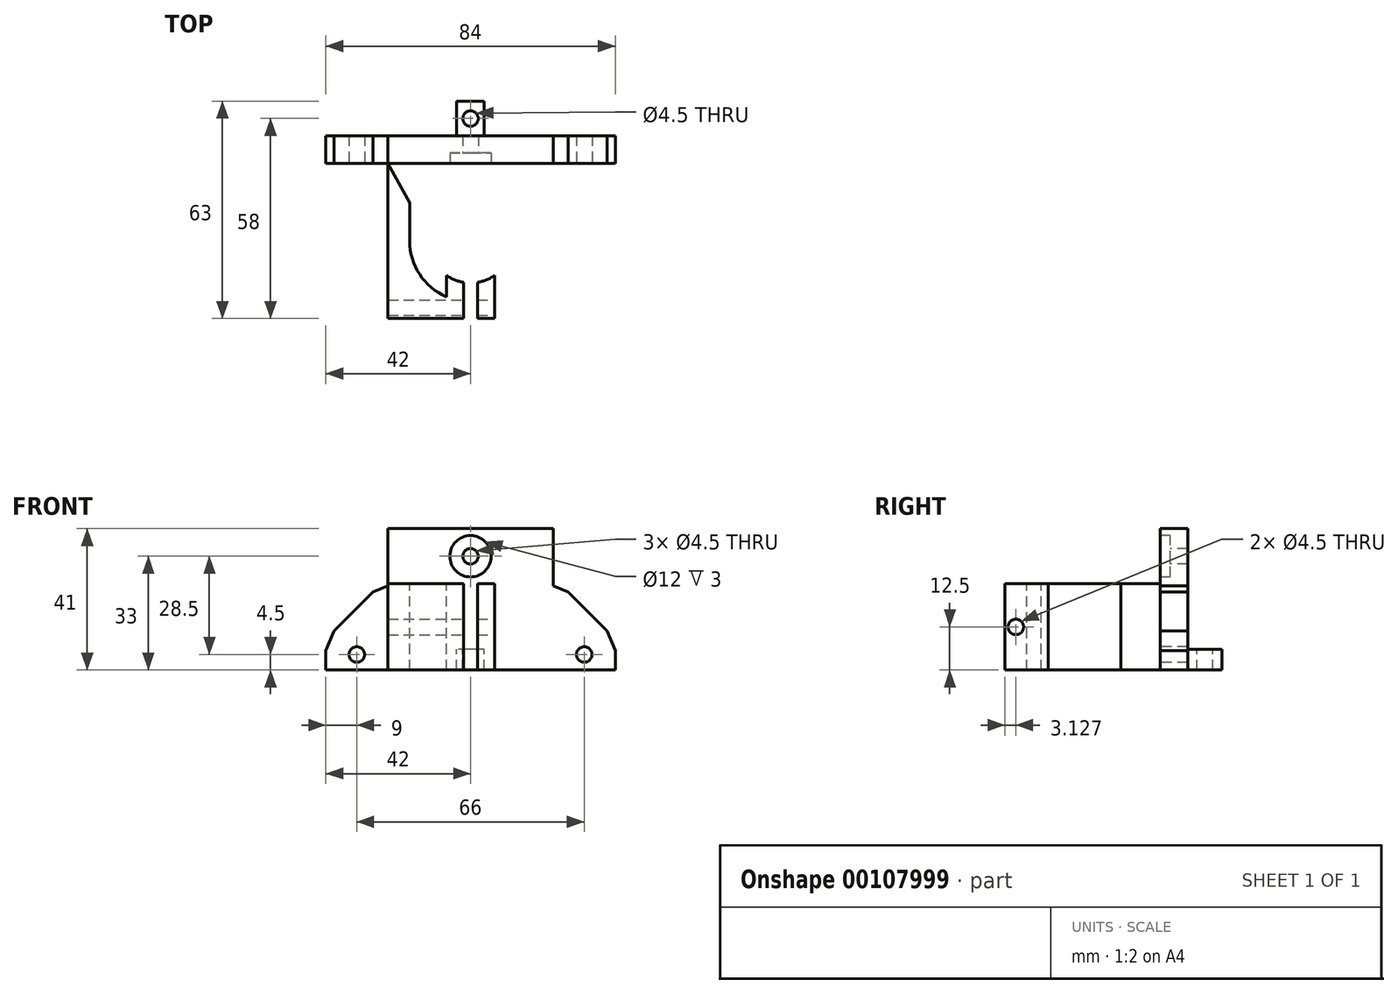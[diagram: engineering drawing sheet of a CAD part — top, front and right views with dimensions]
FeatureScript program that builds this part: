
annotation { "Feature Type Name" : "Feature", "Feature Type Description" : "" }
export const myFeature = defineFeature(function(context is Context, id is Id, definition is map)
    precondition{}
    {
        {
            var Q0;
            Q0=qCreatedBy(makeId("Front.planeOp"),FACE);
            var sketch = newSketch(context, id + "F0", { "sketchPlane" : qUnion([Q0])});
            skLineSegment(sketch, "E0.bottom", {"start": v(0, 0) * mm, "end": v(48, 0) * mm});
            skLineSegment(sketch, "E0.top", {"start": v(0, 49) * mm, "end": v(48, 49) * mm});
            skLineSegment(sketch, "E0.left", {"start": v(0, 0) * mm, "end": v(0, 49) * mm});
            skLineSegment(sketch, "E0.right", {"start": v(48, 0) * mm, "end": v(48, 49) * mm});
            skSolve(sketch);
        }
        {
            var Q0;
            Q0 = qSketchRegion(id + "F0", true);
            extrude(context, id + "F1", {"entities" : qUnion([Q0]), "depth" : (70 - 25 + 8) * mm});
        }
        {
            var Q0;
            Q0=makeQuery(id+"F1.opExtrude","CAP_FACE",FACE,{"disambiguationData":[OSD([sQuery(id+"F0.wireOp",EDGE,"E0.bottom"),sQuery(id+"F0.wireOp",EDGE,"E0.top"),sQuery(id+"F0.wireOp",EDGE,"E0.left"),sQuery(id+"F0.wireOp",EDGE,"E0.right")])],"isStart":false});
            var sketch = newSketch(context, id + "F2", { "sketchPlane" : qUnion([Q0])});
            skLineSegment(sketch, "E1.bottom", {"start": v(0, 49) * mm, "end": v(48, 49) * mm});
            skLineSegment(sketch, "E1.top", {"start": v(0, 25) * mm, "end": v(48, 25) * mm});
            skLineSegment(sketch, "E1.left", {"start": v(0, 49) * mm, "end": v(0, 25) * mm});
            skLineSegment(sketch, "E1.right", {"start": v(48, 49) * mm, "end": v(48, 25) * mm});
            skSolve(sketch);
        }
        {
            var Q0;
            Q0 = qSketchRegion(id + "F2", true);
            extrude(context, id + "F3", {"entities" : qUnion([Q0]), "operationType" : NewBodyOperationType.REMOVE, "oppositeDirection" : true, "depth" : 45 * mm});
        }
        {
            var Q0;
            Q0=makeQuery(id+"F3.boolean.opBoolean","COPY",FACE,{"derivedFrom":makeQuery(id+"F3.opExtrude","SWEPT_FACE",FACE,{"disambiguationData":[OSD([sQuery(id+"F2.wireOp",EDGE,"E1.top")])]})});
            var sketch = newSketch(context, id + "F4", { "sketchPlane" : qUnion([Q0])});
            skCircle(sketch, "E2", {"center": v(24, -30.5) * mm, "radius": 12.2 * mm});
            skLineSegment(sketch, "E3", {"start": v(24, -8) * mm, "end": v(24, -53) * mm, "construction": true});
            skLineSegment(sketch, "E4", {"start": v(0, -30.5) * mm, "end": v(48, -30.5) * mm, "construction": true});
            skLineSegment(sketch, "E5.bottom", {"start": v(22, -53) * mm, "end": v(26, -53) * mm});
            skLineSegment(sketch, "E5.top", {"start": v(22, -42.53) * mm, "end": v(26, -42.53) * mm});
            skLineSegment(sketch, "E5.left", {"start": v(22, -53) * mm, "end": v(22, -42.53) * mm});
            skLineSegment(sketch, "E5.right", {"start": v(26, -53) * mm, "end": v(26, -42.53) * mm});
            skLineSegment(sketch, "E6", {"start": v(17, -40.5) * mm, "end": v(31, -40.5) * mm});
            skLineSegment(sketch, "E7.bottom", {"start": v(17, -53) * mm, "end": v(31, -53) * mm});
            skLineSegment(sketch, "E7.left", {"start": v(17, -53) * mm, "end": v(17, -40.5) * mm});
            skLineSegment(sketch, "E7.right", {"start": v(31, -53) * mm, "end": v(31, -40.5) * mm});
            skPoint(sketch, "E8", {"position": v(11.8, -30.5) * mm});
            skPoint(sketch, "E9", {"position": v(36.2, -30.5) * mm});
            skArc(sketch, "E10", {"start": v(17, -46.75) * mm, "mid": v(9.22, -40.22) * mm, "end": v(6.31, -30.5) * mm});
            skArc(sketch, "E11", {"start": v(31, -46.75) * mm, "mid": v(38.78, -40.22) * mm, "end": v(41.69, -30.5) * mm});
            skLineSegment(sketch, "E12", {"start": v(6.31, -19.42) * mm, "end": v(0, -8) * mm});
            skLineSegment(sketch, "E13", {"start": v(6.31, -19.42) * mm, "end": v(6.31, -30.5) * mm});
            skLineSegment(sketch, "E14", {"start": v(48, -8) * mm, "end": v(41.69, -19.42) * mm});
            skLineSegment(sketch, "E15", {"start": v(41.69, -19.42) * mm, "end": v(41.69, -30.5) * mm});
            skSolve(sketch);
        }
        {
            var Q0;
            {var subQ0=sQuery(id+"F4.wireOp",EDGE,"E6");Q0=makeQuery(id+"F4.imprint","IMPRINT",FACE,{"disambiguationData":[TD([[makeQuery(id+"F4.imprint","IMPRINT",EDGE,{"derivedFrom":subQ0}),1.0]])]});}
            var Q1;
            {var subQ0=sQuery(id+"F4.wireOp",EDGE,"E5.top");Q1=makeQuery(id+"F4.imprint","IMPRINT",FACE,{"disambiguationData":[TD([[makeQuery(id+"F4.imprint","IMPRINT",EDGE,{"derivedFrom":subQ0}),1.0]])]});}
            var Q2;
            {var subQ0=sQuery(id+"F4.wireOp",EDGE,"E5.left");Q2=makeQuery(id+"F4.imprint","IMPRINT",FACE,{"disambiguationData":[TD([[makeQuery(id+"F4.imprint","IMPRINT",EDGE,{"derivedFrom":subQ0}),-1.0]])]});}
            var Q3;
            {var subQ2=sQuery(id+"F4.wireOp",EDGE,"E10");Q3=makeQuery(id+"F4.imprint","IMPRINT",FACE,{"disambiguationData":[TD([[makeQuery(id+"F4.imprint","IMPRINT",EDGE,{"derivedFrom":subQ2}),1.0]])]});}
            var Q4;
            {var subQ5=sQuery(id+"F4.wireOp",EDGE,"E11");Q4=makeQuery(id+"F4.imprint","IMPRINT",FACE,{"disambiguationData":[TD([[makeQuery(id+"F4.imprint","IMPRINT",EDGE,{"derivedFrom":subQ5}),-1.0]])]});}
            var Q5;
            {var subQ0=sQuery(id+"F4.wireOp",EDGE,"E5.top");Q5=makeQuery(id+"F4.imprint","IMPRINT",FACE,{"disambiguationData":[TD([[makeQuery(id+"F4.imprint","IMPRINT",EDGE,{"derivedFrom":subQ0}),-1.0]])]});}
            extrude(context, id + "F5", {"entities" : qUnion([Q0, Q1, Q2, Q3, Q4, Q5]), "operationType" : NewBodyOperationType.REMOVE, "oppositeDirection" : true, "depth" : 25 * mm});
        }
        {
            var Q0;
            Q0=makeQuery(id+"F1.opExtrude","CAP_FACE",FACE,{"disambiguationData":[OSD([sQuery(id+"F0.wireOp",EDGE,"E0.bottom"),sQuery(id+"F0.wireOp",EDGE,"E0.top"),sQuery(id+"F0.wireOp",EDGE,"E0.left"),sQuery(id+"F0.wireOp",EDGE,"E0.right")])],"isStart":true});
            var sketch = newSketch(context, id + "F6", { "sketchPlane" : qUnion([Q0])});
            skLineSegment(sketch, "E16.bottom", {"start": v(-28, 0) * mm, "end": v(-20, 0) * mm});
            skLineSegment(sketch, "E16.top", {"start": v(-28, 6) * mm, "end": v(-20, 6) * mm});
            skLineSegment(sketch, "E16.left", {"start": v(-28, 0) * mm, "end": v(-28, 6) * mm});
            skLineSegment(sketch, "E16.right", {"start": v(-20, 0) * mm, "end": v(-20, 6) * mm});
            skLineSegment(sketch, "E17", {"start": v(-24, 49) * mm, "end": v(-24, 0) * mm, "construction": true});
            skSolve(sketch);
        }
        {
            var Q0;
            Q0=makeQuery(id+"F6.imprint","IMPRINT",FACE,{"disambiguationData":[TD([[makeQuery(id+"F6.imprint","IMPRINT",EDGE,{"derivedFrom":sQuery(id+"F6.wireOp",EDGE,"E16.bottom")}),-1.0]])]});
            extrude(context, id + "F7", {"entities" : qUnion([Q0]), "operationType" : NewBodyOperationType.ADD, "depth" : 10 * mm});
        }
        {
            var Q0;
            Q0=makeQuery(id+"F1.opExtrude","SWEPT_FACE",FACE,{"disambiguationData":[OSD([sQuery(id+"F0.wireOp",EDGE,"E0.top")])]});
            extrude(context, id + "F8", {"entities" : qUnion([Q0]), "operationType" : NewBodyOperationType.REMOVE, "oppositeDirection" : true, "depth" : 8 * mm});
        }
        {
            var Q0;
            Q0=makeQuery(id+"F3.boolean.opBoolean","COPY",FACE,{"derivedFrom":makeQuery(id+"F3.opExtrude","CAP_FACE",FACE,{"disambiguationData":[OSD([sQuery(id+"F2.wireOp",EDGE,"E1.bottom"),sQuery(id+"F2.wireOp",EDGE,"E1.top"),sQuery(id+"F2.wireOp",EDGE,"E1.left"),sQuery(id+"F2.wireOp",EDGE,"E1.right")])],"isStart":false})});
            var sketch = newSketch(context, id + "F9", { "sketchPlane" : qUnion([Q0])});
            skLineSegment(sketch, "E18", {"start": v(24, 41) * mm, "end": v(24, 25) * mm, "construction": true});
            skLineSegment(sketch, "E19", {"start": v(0, 33) * mm, "end": v(48, 33) * mm, "construction": true});
            skCircle(sketch, "E20", {"center": v(24, 33) * mm, "radius": 2.25 * mm});
            skCircle(sketch, "E21", {"center": v(24, 33) * mm, "radius": 6 * mm});
            skSolve(sketch);
        }
        {
            var Q0;
            Q0=makeQuery(id+"F9.imprint","IMPRINT",FACE,{"disambiguationData":[TD([[makeQuery(id+"F9.imprint","IMPRINT",EDGE,{"derivedFrom":sQuery(id+"F9.wireOp",EDGE,"E20")}),1.0]])]});
            extrude(context, id + "F10", {"entities" : qUnion([Q0]), "operationType" : NewBodyOperationType.REMOVE, "endBound" : BoundingType.THROUGH_ALL, "oppositeDirection" : true, "depth" : 25 * mm});
        }
        {
            var Q0;
            Q0=makeQuery(id+"F9.imprint","IMPRINT",FACE,{"disambiguationData":[TD([[makeQuery(id+"F9.imprint","IMPRINT",EDGE,{"derivedFrom":sQuery(id+"F9.wireOp",EDGE,"E20")}),-1.0]])]});
            extrude(context, id + "F11", {"entities" : qUnion([Q0]), "operationType" : NewBodyOperationType.REMOVE, "oppositeDirection" : true, "depth" : 3 * mm});
        }
        {
            var Q0;
            Q0=makeQuery(id+"F7.opExtrude","SWEPT_FACE",FACE,{"disambiguationData":[OSD([sQuery(id+"F6.wireOp",EDGE,"E16.top")])]});
            var sketch = newSketch(context, id + "F12", { "sketchPlane" : qUnion([Q0])});
            skLineSegment(sketch, "E22", {"start": v(20, 0) * mm, "end": v(28, 10) * mm, "construction": true});
            skCircle(sketch, "E23", {"center": v(24, 5) * mm, "radius": 2.25 * mm});
            skSolve(sketch);
        }
        {
            var Q0;
            Q0=makeQuery(id+"F12.imprint","IMPRINT",FACE,{"disambiguationData":[TD([[makeQuery(id+"F12.imprint","IMPRINT",EDGE,{"derivedFrom":sQuery(id+"F12.wireOp",EDGE,"E23")}),1.0]])]});
            extrude(context, id + "F13", {"entities" : qUnion([Q0]), "operationType" : NewBodyOperationType.REMOVE, "endBound" : BoundingType.THROUGH_ALL, "oppositeDirection" : true, "depth" : 25 * mm});
        }
        {
            var Q0;
            Q0=makeQuery(id+"F1.opExtrude","SWEPT_FACE",FACE,{"disambiguationData":[OSD([sQuery(id+"F0.wireOp",EDGE,"E0.right")])]});
            var sketch = newSketch(context, id + "F14", { "sketchPlane" : qUnion([Q0])});
            skLineSegment(sketch, "E24.bottom", {"start": v(-8, 25) * mm, "end": v(0, 25) * mm});
            skLineSegment(sketch, "E24.top", {"start": v(-8, 0) * mm, "end": v(0, 0) * mm});
            skLineSegment(sketch, "E24.left", {"start": v(-8, 25) * mm, "end": v(-8, 0) * mm});
            skLineSegment(sketch, "E24.right", {"start": v(0, 25) * mm, "end": v(0, 0) * mm});
            skSolve(sketch);
        }
        {
            var Q0;
            Q0=makeQuery(id+"F14.imprint","IMPRINT",FACE,{"disambiguationData":[TD([[makeQuery(id+"F14.imprint","IMPRINT",EDGE,{"derivedFrom":sQuery(id+"F14.wireOp",EDGE,"E24.bottom")}),-1.0]])]});
            extrude(context, id + "F15", {"entities" : qUnion([Q0]), "operationType" : NewBodyOperationType.ADD, "depth" : 18 * mm});
        }
        {
            var Q0;
            Q0=makeQuery(id+"F1.opExtrude","SWEPT_FACE",FACE,{"disambiguationData":[OSD([sQuery(id+"F0.wireOp",EDGE,"E0.left")])]});
            var sketch = newSketch(context, id + "F16", { "sketchPlane" : qUnion([Q0])});
            skLineSegment(sketch, "E25.bottom", {"start": v(8, 25) * mm, "end": v(0, 25) * mm});
            skLineSegment(sketch, "E25.top", {"start": v(8, 0) * mm, "end": v(0, 0) * mm});
            skLineSegment(sketch, "E25.left", {"start": v(8, 25) * mm, "end": v(8, 0) * mm});
            skLineSegment(sketch, "E25.right", {"start": v(0, 25) * mm, "end": v(0, 0) * mm});
            skSolve(sketch);
        }
        {
            var Q0;
            Q0=makeQuery(id+"F16.imprint","IMPRINT",FACE,{"disambiguationData":[TD([[makeQuery(id+"F16.imprint","IMPRINT",EDGE,{"derivedFrom":sQuery(id+"F16.wireOp",EDGE,"E25.bottom")}),1.0]])]});
            extrude(context, id + "F17", {"entities" : qUnion([Q0]), "operationType" : NewBodyOperationType.ADD, "depth" : 18 * mm});
        }
        {
            var Q0;
            Q0=makeQuery(id+"F17.opExtrude","CAP_EDGE",EDGE,{"disambiguationData":[OSD([sQuery(id+"F16.wireOp",EDGE,"E25.bottom")])],"isStart":false});
            var Q1;
            Q1=makeQuery(id+"F8.boolean.opBoolean","COPY",EDGE,{"derivedFrom":makeQuery(id+"F8.opExtrude","CAP_EDGE",EDGE,{"disambiguationData":[OSD([sQuery(id+"F0.wireOp",EDGE,"E0.top"),sQuery(id+"F0.wireOp",EDGE,"E0.left")])],"isStart":false})});
            var Q2;
            Q2=makeQuery(id+"F8.boolean.opBoolean","COPY",EDGE,{"derivedFrom":makeQuery(id+"F8.opExtrude","CAP_EDGE",EDGE,{"disambiguationData":[OSD([sQuery(id+"F0.wireOp",EDGE,"E0.top"),sQuery(id+"F0.wireOp",EDGE,"E0.right")])],"isStart":false})});
            var Q3;
            Q3=makeQuery(id+"F15.opExtrude","CAP_EDGE",EDGE,{"disambiguationData":[OSD([sQuery(id+"F14.wireOp",EDGE,"E24.bottom")])],"isStart":false});
            chamfer(context, id + "F18", {"entities" : qUnion([Q0, Q1, Q2, Q3]), "width" : 16 * mm, "tangentPropagation" : true});
        }
        {
            var Q0;
            Q0=makeQuery(id+"F17.opExtrude","SWEPT_FACE",FACE,{"disambiguationData":[OSD([sQuery(id+"F16.wireOp",EDGE,"E25.left")])]});
            var sketch = newSketch(context, id + "F19", { "sketchPlane" : qUnion([Q0])});
            skLineSegment(sketch, "E26", {"start": v(-18, 9) * mm, "end": v(0, 0) * mm, "construction": true});
            skCircle(sketch, "E27", {"center": v(-9, 4.5) * mm, "radius": 2.25 * mm});
            skSolve(sketch);
        }
        {
            var Q0;
            Q0=makeQuery(id+"F19.imprint","IMPRINT",FACE,{"disambiguationData":[TD([[makeQuery(id+"F19.imprint","IMPRINT",EDGE,{"derivedFrom":sQuery(id+"F19.wireOp",EDGE,"E27")}),1.0]])]});
            extrude(context, id + "F20", {"entities" : qUnion([Q0]), "operationType" : NewBodyOperationType.REMOVE, "endBound" : BoundingType.THROUGH_ALL, "oppositeDirection" : true, "depth" : 25 * mm});
        }
        {
            var Q0;
            Q0=makeQuery(id+"F15.opExtrude","SWEPT_FACE",FACE,{"disambiguationData":[OSD([sQuery(id+"F14.wireOp",EDGE,"E24.left")])]});
            var sketch = newSketch(context, id + "F21", { "sketchPlane" : qUnion([Q0])});
            skLineSegment(sketch, "E28", {"start": v(48, 0) * mm, "end": v(66, 9) * mm, "construction": true});
            skCircle(sketch, "E29", {"center": v(57, 4.5) * mm, "radius": 2.25 * mm});
            skSolve(sketch);
        }
        {
            var Q0;
            Q0=makeQuery(id+"F21.imprint","IMPRINT",FACE,{"disambiguationData":[TD([[makeQuery(id+"F21.imprint","IMPRINT",EDGE,{"derivedFrom":sQuery(id+"F21.wireOp",EDGE,"E29")}),1.0]])]});
            extrude(context, id + "F22", {"entities" : qUnion([Q0]), "operationType" : NewBodyOperationType.REMOVE, "endBound" : BoundingType.THROUGH_ALL, "oppositeDirection" : true, "depth" : 25 * mm});
        }
        {
            var Q0;
            {var subQ0=sQuery(id+"F16.wireOp",EDGE,"E25.bottom");Q0=makeQuery(id+"F18.opChamfer","BLEND_EDGE",EDGE,{"blendedFrom":[makeQuery(id+"F17.opExtrude","CAP_EDGE",EDGE,{"disambiguationData":[OSD([subQ0])],"isStart":false}),makeQuery(id+"F17.opExtrude","CAP_FACE",FACE,{"disambiguationData":[OSD([subQ0,sQuery(id+"F16.wireOp",EDGE,"E25.top"),sQuery(id+"F16.wireOp",EDGE,"E25.left"),sQuery(id+"F16.wireOp",EDGE,"E25.right")])],"isStart":false})],"blendedInto":[makeQuery(id+"F17.opExtrude","CAP_FACE",FACE,{"disambiguationData":[OSD([subQ0,sQuery(id+"F16.wireOp",EDGE,"E25.top"),sQuery(id+"F16.wireOp",EDGE,"E25.left"),sQuery(id+"F16.wireOp",EDGE,"E25.right")])],"isStart":false})]});}
            var Q1;
            {var subQ0=sQuery(id+"F14.wireOp",EDGE,"E24.bottom");Q1=makeQuery(id+"F18.opChamfer","BLEND_EDGE",EDGE,{"blendedFrom":[makeQuery(id+"F15.opExtrude","CAP_EDGE",EDGE,{"disambiguationData":[OSD([subQ0])],"isStart":false}),makeQuery(id+"F15.opExtrude","CAP_FACE",FACE,{"disambiguationData":[OSD([subQ0,sQuery(id+"F14.wireOp",EDGE,"E24.top"),sQuery(id+"F14.wireOp",EDGE,"E24.left"),sQuery(id+"F14.wireOp",EDGE,"E24.right")])],"isStart":false})],"blendedInto":[makeQuery(id+"F15.opExtrude","CAP_FACE",FACE,{"disambiguationData":[OSD([subQ0,sQuery(id+"F14.wireOp",EDGE,"E24.top"),sQuery(id+"F14.wireOp",EDGE,"E24.left"),sQuery(id+"F14.wireOp",EDGE,"E24.right")])],"isStart":false})]});}
            var Q2;
            {var subQ0=sQuery(id+"F14.wireOp",EDGE,"E24.bottom");Q2=makeQuery(id+"F18.opChamfer","BLEND_EDGE",EDGE,{"blendedFrom":[makeQuery(id+"F15.opExtrude","CAP_EDGE",EDGE,{"disambiguationData":[OSD([subQ0])],"isStart":false}),makeQuery(id+"F15.opExtrude","SWEPT_FACE",FACE,{"disambiguationData":[OSD([subQ0])]})],"blendedInto":[makeQuery(id+"F15.opExtrude","SWEPT_FACE",FACE,{"disambiguationData":[OSD([subQ0])]})]});}
            var Q3;
            {var subQ0=sQuery(id+"F16.wireOp",EDGE,"E25.bottom");Q3=makeQuery(id+"F18.opChamfer","BLEND_EDGE",EDGE,{"blendedFrom":[makeQuery(id+"F17.opExtrude","CAP_EDGE",EDGE,{"disambiguationData":[OSD([subQ0])],"isStart":false}),makeQuery(id+"F17.opExtrude","SWEPT_FACE",FACE,{"disambiguationData":[OSD([subQ0])]})],"blendedInto":[makeQuery(id+"F17.opExtrude","SWEPT_FACE",FACE,{"disambiguationData":[OSD([subQ0])]})]});}
            var Q4;
            {var subQ0=sQuery(id+"F0.wireOp",EDGE,"E0.top");Q4=makeQuery(id+"F18.opChamfer","BLEND_EDGE",EDGE,{"blendedFrom":[makeQuery(id+"F8.boolean.opBoolean","COPY",EDGE,{"derivedFrom":makeQuery(id+"F8.opExtrude","CAP_EDGE",EDGE,{"disambiguationData":[OSD([subQ0,sQuery(id+"F0.wireOp",EDGE,"E0.left")])],"isStart":false})}),makeQuery(id+"F8.boolean.opBoolean","COPY",FACE,{"derivedFrom":makeQuery(id+"F8.opExtrude","CAP_FACE",FACE,{"disambiguationData":[OSD([subQ0])],"isStart":false})})],"blendedInto":[makeQuery(id+"F8.boolean.opBoolean","COPY",FACE,{"derivedFrom":makeQuery(id+"F8.opExtrude","CAP_FACE",FACE,{"disambiguationData":[OSD([subQ0])],"isStart":false})})]});}
            var Q5;
            {var subQ0=sQuery(id+"F0.wireOp",EDGE,"E0.top");Q5=makeQuery(id+"F18.opChamfer","BLEND_EDGE",EDGE,{"blendedFrom":[makeQuery(id+"F8.boolean.opBoolean","COPY",EDGE,{"derivedFrom":makeQuery(id+"F8.opExtrude","CAP_EDGE",EDGE,{"disambiguationData":[OSD([subQ0,sQuery(id+"F0.wireOp",EDGE,"E0.right")])],"isStart":false})}),makeQuery(id+"F8.boolean.opBoolean","COPY",FACE,{"derivedFrom":makeQuery(id+"F8.opExtrude","CAP_FACE",FACE,{"disambiguationData":[OSD([subQ0])],"isStart":false})})],"blendedInto":[makeQuery(id+"F8.boolean.opBoolean","COPY",FACE,{"derivedFrom":makeQuery(id+"F8.opExtrude","CAP_FACE",FACE,{"disambiguationData":[OSD([subQ0])],"isStart":false})})]});}
            chamfer(context, id + "F23", {"entities" : qUnion([Q0, Q1, Q2, Q3, Q4, Q5]), "width" : 8 * mm, "tangentPropagation" : true});
        }
        {
            var Q0;
            Q0=makeQuery(id+"F5.boolean.opBoolean","COPY",FACE,{"derivedFrom":makeQuery(id+"F5.opExtrude","SWEPT_FACE",FACE,{"disambiguationData":[OSD([sQuery(id+"F4.wireOp",EDGE,"E7.right")])]})});
            var sketch = newSketch(context, id + "F24", { "sketchPlane" : qUnion([Q0])});
            skCircle(sketch, "E30", {"center": v(-49.87, 12.5) * mm, "radius": 2.25 * mm});
            skPoint(sketch, "E30.centerSnap0", {"position": v(-53, 12.5) * mm});
            skPoint(sketch, "E30.centerSnap1", {"position": v(-49.87, 25) * mm});
            skSolve(sketch);
        }
        {
            var Q0;
            Q0 = qSketchRegion(id + "F24", true);
            extrude(context, id + "F25", {"entities" : qUnion([Q0]), "operationType" : NewBodyOperationType.REMOVE, "endBound" : BoundingType.THROUGH_ALL, "oppositeDirection" : true, "depth" : 25 * mm});
        }
    });
